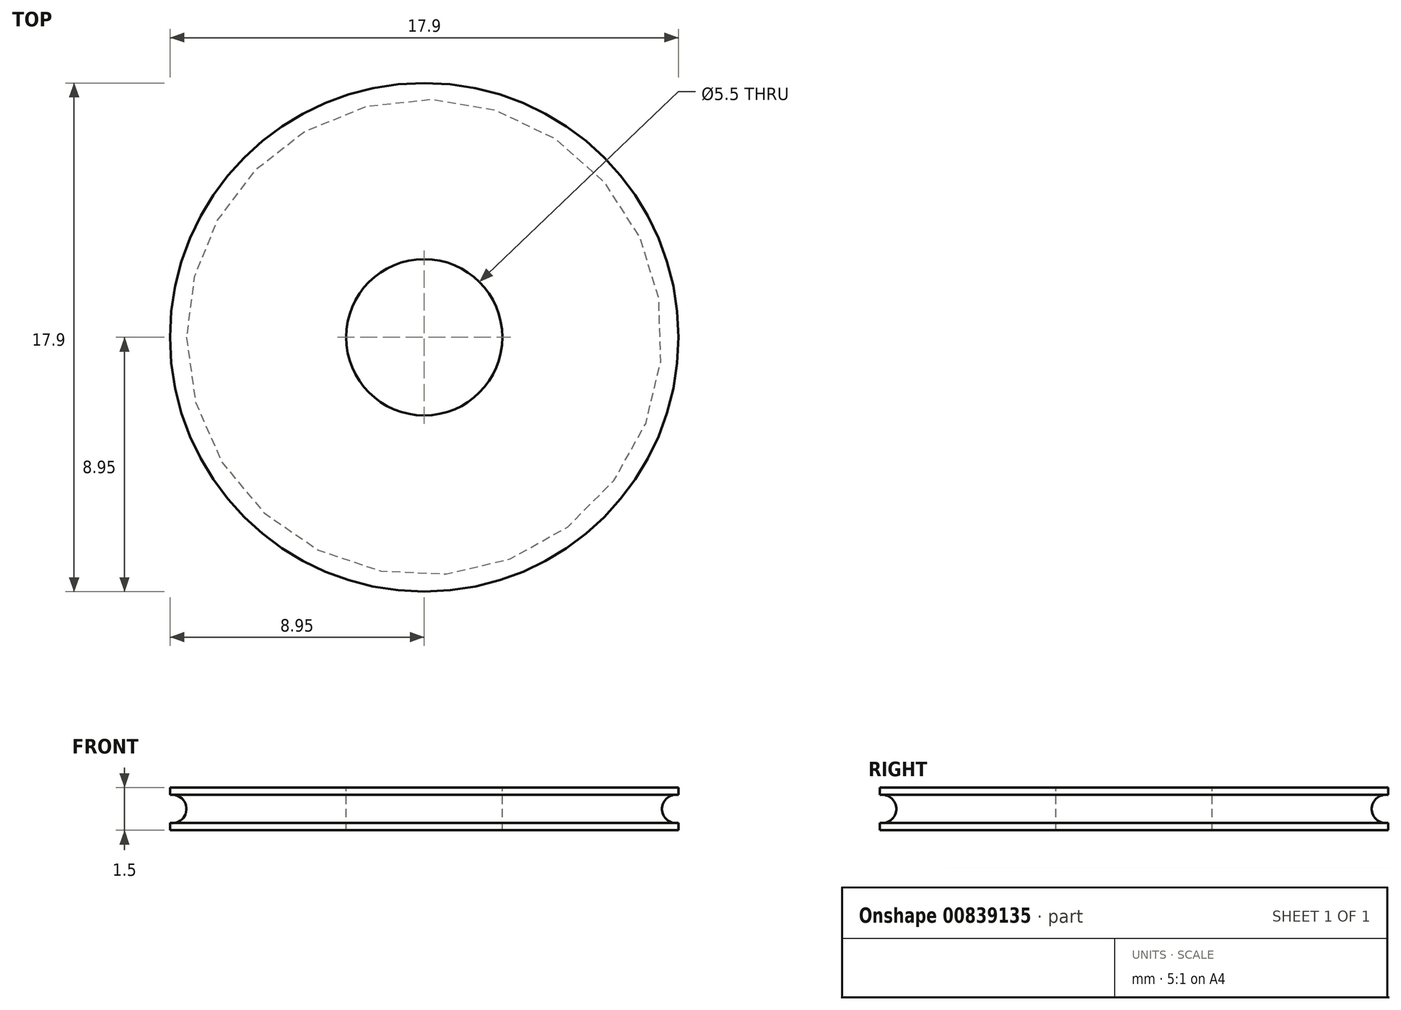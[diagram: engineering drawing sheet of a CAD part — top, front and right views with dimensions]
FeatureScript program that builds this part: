
annotation { "Feature Type Name" : "Feature", "Feature Type Description" : "" }
export const myFeature = defineFeature(function(context is Context, id is Id, definition is map)
    precondition{}
    {
        {
            var Q0;
            Q0=qCreatedBy(makeId("Top.planeOp"),FACE);
            var sketch = newSketch(context, id + "F0", { "sketchPlane" : qUnion([Q0])});
            skCircle(sketch, "E0", {"center": v(0, 0) * mm, "radius": 8.95 * mm});
            skSolve(sketch);
        }
        {
            var Q0;
            Q0=makeQuery(id+"F0.imprint","IMPRINT",FACE,{"disambiguationData":[TD([[makeQuery(id+"F0.imprint","IMPRINT",EDGE,{"derivedFrom":sQuery(id+"F0.wireOp",EDGE,"E0")}),1.0]])]});
            extrude(context, id + "F1", {"entities" : qUnion([Q0]), "oppositeDirection" : true, "depth" : 0.75 * mm, "offsetDistance" : 25 * mm, "hasSecondDirection" : true, "secondDirectionOppositeDirection" : false, "secondDirectionDepth" : 0.75 * mm});
        }
        {
            var Q0;
            Q0=qCreatedBy(makeId("Front.planeOp"),FACE);
            var sketch = newSketch(context, id + "F2", { "sketchPlane" : qUnion([Q0])});
            skCircle(sketch, "E1", {"center": v(-8.87, 0) * mm, "radius": 0.5 * mm});
            skLineSegment(sketch, "E2", {"start": v(0, 1.96) * mm, "end": v(0, -2.57) * mm, "construction": true});
            skSolve(sketch);
        }
        {
            var Q0;
            Q0 = qSketchRegion(id + "F2", true);
            var Q1;
            Q1=sQuery(id+"F2.wireOp",EDGE,"E2");
            revolve(context, id + "F3", {"operationType" : NewBodyOperationType.REMOVE, "surfaceOperationType" : NewSurfaceOperationType.NEW, "entities" : qUnion([Q0]), "axis" : qUnion([Q1]), "revolveType" : RevolveType.FULL, "oppositeDirection" : true});
        }
        {
            var Q0;
            Q0=qCreatedBy(makeId("Top.planeOp"),FACE);
            var sketch = newSketch(context, id + "F4", { "sketchPlane" : qUnion([Q0])});
            skCircle(sketch, "E3", {"center": v(0, 0) * mm, "radius": 2.75 * mm});
            skSolve(sketch);
        }
        {
            var Q0;
            Q0 = qSketchRegion(id + "F4", true);
            extrude(context, id + "F5", {"entities" : qUnion([Q0]), "operationType" : NewBodyOperationType.REMOVE, "oppositeDirection" : true, "depth" : 30.7 * mm, "offsetDistance" : 25 * mm, "hasSecondDirection" : true, "secondDirectionOppositeDirection" : false, "secondDirectionDepth" : 27 * mm});
        }
    });
